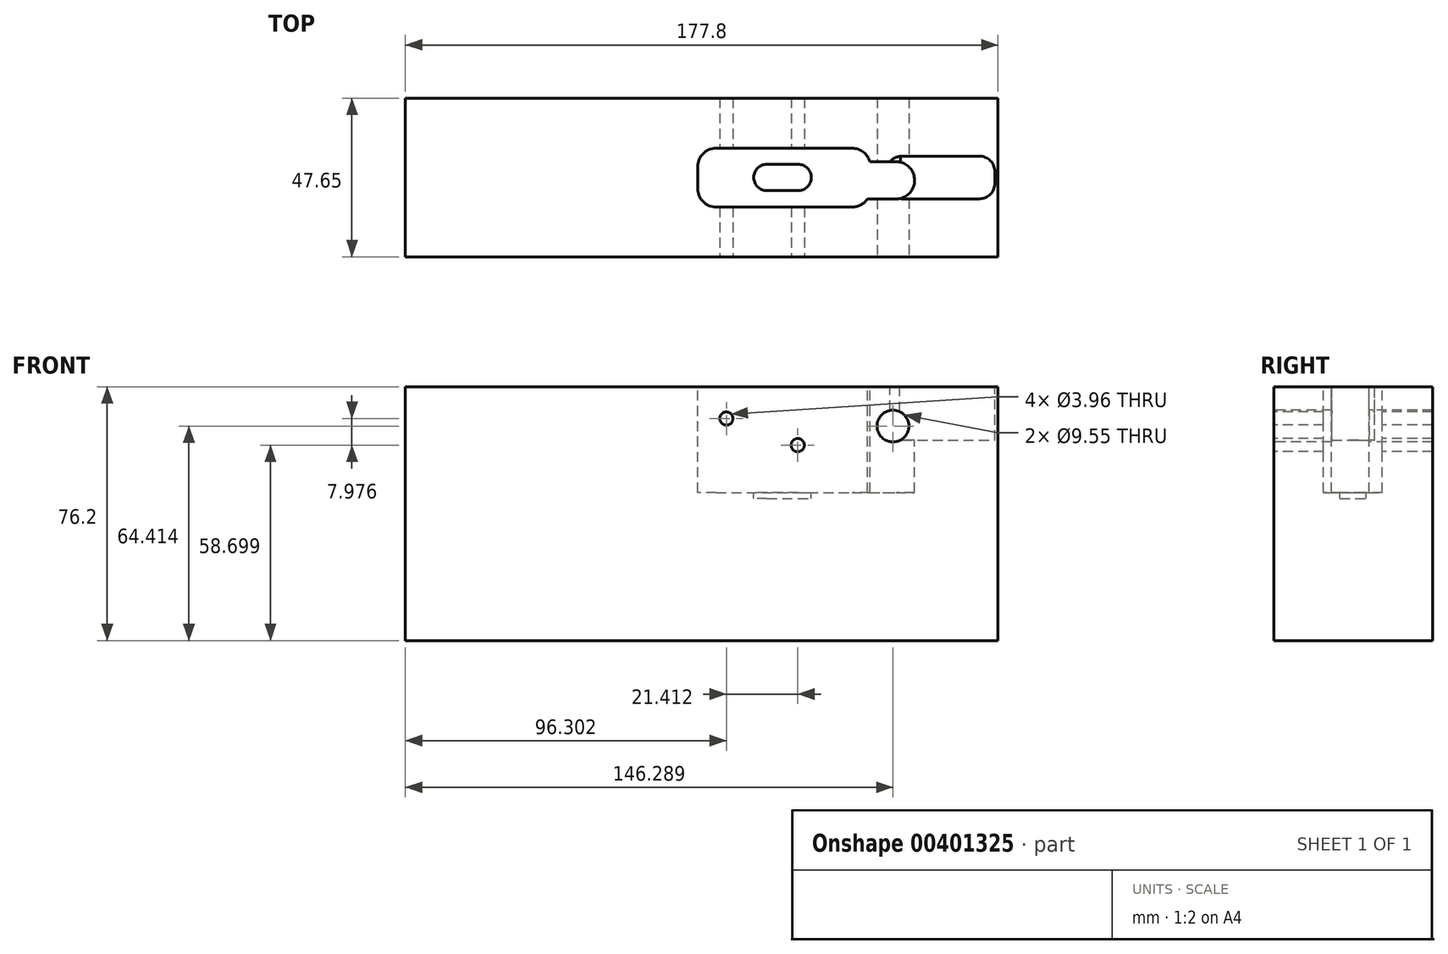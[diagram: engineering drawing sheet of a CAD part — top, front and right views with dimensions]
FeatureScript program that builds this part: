
annotation { "Feature Type Name" : "Feature", "Feature Type Description" : "" }
export const myFeature = defineFeature(function(context is Context, id is Id, definition is map)
    precondition{}
    {
        {
            var Q0;
            Q0=qCreatedBy(makeId("Top.planeOp"),FACE);
            var sketch = newSketch(context, id + "F0", { "sketchPlane" : qUnion([Q0])});
            skLineSegment(sketch, "E0.bottom", {"start": v(-4.76, 47.65) * mm, "end": v(173.04, 47.65) * mm});
            skLineSegment(sketch, "E0.top", {"start": v(-4.76, 0) * mm, "end": v(173.04, 0) * mm});
            skLineSegment(sketch, "E0.left", {"start": v(-4.76, 47.65) * mm, "end": v(-4.76, 0) * mm});
            skLineSegment(sketch, "E0.right", {"start": v(173.04, 47.65) * mm, "end": v(173.04, 0) * mm});
            skLineSegment(sketch, "E1", {"start": v(173, 23.83) * mm, "end": v(-20.73, 23.83) * mm, "construction": true});
            skPoint(sketch, "E1.startSnap0", {"position": v(173.04, 23.83) * mm});
            skPoint(sketch, "E1.endSnap0", {"position": v(-4.76, 23.83) * mm});
            skSolve(sketch);
        }
        {
            var Q0;
            Q0=makeQuery(id+"F0.imprint","IMPRINT",FACE,{"disambiguationData":[TD([[makeQuery(id+"F0.imprint","IMPRINT",EDGE,{"derivedFrom":sQuery(id+"F0.wireOp",EDGE,"E0.bottom")}),-1.0]])]});
            extrude(context, id + "F1", {"entities" : qUnion([Q0]), "oppositeDirection" : true, "depth" : 76.2 * mm});
        }
        {
            var Q0;
            Q0=qCreatedBy(makeId("Front.planeOp"),FACE);
            var sketch = newSketch(context, id + "F2", { "sketchPlane" : qUnion([Q0])});
            skCircle(sketch, "E2", {"center": v(0, 0) * mm, "radius": 3.18 * mm, "construction": true});
            skCircle(sketch, "E3", {"center": v(141.53, -11.79) * mm, "radius": 4.78 * mm});
            skCircle(sketch, "E4", {"center": v(112.95, -17.5) * mm, "radius": 1.98 * mm});
            skCircle(sketch, "E5", {"center": v(91.54, -9.52) * mm, "radius": 1.98 * mm});
            skSolve(sketch);
        }
        {
            var Q0;
            Q0=qSketchRegion(id+"F2",true);
            extrude(context, id + "F3", {"entities" : qUnion([Q0]), "operationType" : NewBodyOperationType.REMOVE, "endBound" : BoundingType.THROUGH_ALL, "oppositeDirection" : true, "depth" : 25.4 * mm});
        }
        {
            var Q0;
            Q0=makeQuery(id+"F0.imprint","IMPRINT",FACE,{"disambiguationData":[TD([[makeQuery(id+"F0.imprint","IMPRINT",EDGE,{"derivedFrom":sQuery(id+"F0.wireOp",EDGE,"E0.bottom")}),-1.0]])]});
            var sketch = newSketch(context, id + "F4", { "sketchPlane" : qUnion([Q0])});
            skLineSegment(sketch, "E6.right", {"start": v(172.14, 25.46) * mm, "end": v(172.14, 22.19) * mm});
            skPoint(sketch, "E7.visualSharp", {"position": v(172.14, 30.23) * mm});
            skPoint(sketch, "E8.visualSharp", {"position": v(172.14, 17.42) * mm});
            skPoint(sketch, "E9.visualSharp", {"position": v(142.53, 46.05) * mm});
            skLineSegment(sketch, "E10", {"start": v(144.26, 30.23) * mm, "end": v(167.37, 30.23) * mm});
            skLineSegment(sketch, "E11", {"start": v(0, 63.67) * mm, "end": v(0, 0) * mm, "construction": true});
            skLineSegment(sketch, "E12", {"start": v(139.5, 25.46) * mm, "end": v(139.5, 22.19) * mm});
            skLineSegment(sketch, "E13", {"start": v(144.26, 17.42) * mm, "end": v(167.37, 17.42) * mm});
            skPoint(sketch, "E14.visualSharp", {"position": v(139.5, 30.23) * mm});
            skPoint(sketch, "E15.visualSharp", {"position": v(139.5, 17.42) * mm});
            skArc(sketch, "E16.filletArc", {"start": v(144.26, 30.23) * mm, "mid": v(140.9, 28.83) * mm, "end": v(139.5, 25.46) * mm});
            skArc(sketch, "E17.filletArc", {"start": v(139.5, 22.19) * mm, "mid": v(140.9, 18.82) * mm, "end": v(144.26, 17.42) * mm});
            skArc(sketch, "E18.filletArc", {"start": v(167.37, 17.42) * mm, "mid": v(170.74, 18.82) * mm, "end": v(172.14, 22.19) * mm});
            skArc(sketch, "E19.filletArc", {"start": v(172.14, 25.46) * mm, "mid": v(170.74, 28.83) * mm, "end": v(167.37, 30.23) * mm});
            skSolve(sketch);
        }
        {
            var Q0;
            Q0=qSketchRegion(id+"F4",true);
            extrude(context, id + "F5", {"entities" : qUnion([Q0]), "operationType" : NewBodyOperationType.REMOVE, "oppositeDirection" : true, "depth" : 16 * mm});
        }
        {
            var Q0;
            Q0=makeQuery(id+"F0.imprint","IMPRINT",FACE,{"disambiguationData":[TD([[makeQuery(id+"F0.imprint","IMPRINT",EDGE,{"derivedFrom":sQuery(id+"F0.wireOp",EDGE,"E0.bottom")}),-1.0]])]});
            var sketch = newSketch(context, id + "F6", { "sketchPlane" : qUnion([Q0])});
            skLineSegment(sketch, "E20.bottom", {"start": v(103.7, 27.78) * mm, "end": v(113.06, 27.78) * mm});
            skLineSegment(sketch, "E20.top", {"start": v(103.7, 19.86) * mm, "end": v(113.06, 19.86) * mm});
            skLineSegment(sketch, "E20.left", {"start": v(99.75, 23.82) * mm, "end": v(99.75, 23.82) * mm});
            skLineSegment(sketch, "E20.right", {"start": v(117.02, 23.82) * mm, "end": v(117.02, 23.82) * mm});
            skPoint(sketch, "E21.visualSharp", {"position": v(99.75, 27.78) * mm});
            skArc(sketch, "E21.filletArc", {"start": v(103.7, 27.78) * mm, "mid": v(100.9, 26.62) * mm, "end": v(99.75, 23.82) * mm});
            skPoint(sketch, "E22.visualSharp", {"position": v(117.02, 27.78) * mm});
            skArc(sketch, "E22.filletArc", {"start": v(117.02, 23.82) * mm, "mid": v(115.86, 26.62) * mm, "end": v(113.06, 27.78) * mm});
            skPoint(sketch, "E23.visualSharp", {"position": v(117.02, 19.86) * mm});
            skArc(sketch, "E23.filletArc", {"start": v(113.06, 19.86) * mm, "mid": v(115.86, 21.02) * mm, "end": v(117.02, 23.82) * mm});
            skPoint(sketch, "E24.visualSharp", {"position": v(99.75, 19.86) * mm});
            skArc(sketch, "E24.filletArc", {"start": v(99.75, 23.82) * mm, "mid": v(100.9, 21.02) * mm, "end": v(103.7, 19.86) * mm});
            skSolve(sketch);
        }
        {
            var Q0;
            Q0=qSketchRegion(id+"F6",true);
            extrude(context, id + "F7", {"entities" : qUnion([Q0]), "operationType" : NewBodyOperationType.REMOVE, "oppositeDirection" : true, "depth" : 33.53 * mm});
        }
        {
            var Q0;
            Q0=qCreatedBy(makeId("Top.planeOp"),FACE);
            var sketch = newSketch(context, id + "F9", { "sketchPlane" : qUnion([Q0])});
            skLineSegment(sketch, "E25.bottom", {"start": v(134.6, 28.56) * mm, "end": v(142.47, 28.56) * mm});
            skLineSegment(sketch, "E25.top", {"start": v(133.84, 17.38) * mm, "end": v(142.47, 17.38) * mm});
            skLineSegment(sketch, "E25.right", {"start": v(148, 23.06) * mm, "end": v(148, 22.96) * mm});
            skPoint(sketch, "E26.visualSharp", {"position": v(147.96, 28.56) * mm});
            skArc(sketch, "E26.filletArc", {"start": v(148, 23.06) * mm, "mid": v(146.37, 26.95) * mm, "end": v(142.47, 28.56) * mm});
            skPoint(sketch, "E27.visualSharp", {"position": v(148.05, 17.38) * mm});
            skArc(sketch, "E27.filletArc", {"start": v(142.47, 17.38) * mm, "mid": v(146.4, 19.02) * mm, "end": v(148, 22.96) * mm});
            skPoint(sketch, "E28.visualSharp", {"position": v(131.4, 28.56) * mm});
            skPoint(sketch, "E29.visualSharp", {"position": v(131.4, 17.38) * mm});
            skLineSegment(sketch, "E30.bottom", {"start": v(88.47, 32.6) * mm, "end": v(129.26, 32.6) * mm});
            skLineSegment(sketch, "E30.top", {"start": v(88.47, 14.95) * mm, "end": v(129.26, 14.95) * mm});
            skLineSegment(sketch, "E30.left", {"start": v(82.93, 27.07) * mm, "end": v(82.93, 20.5) * mm});
            skArc(sketch, "E31.filletArc", {"start": v(134.6, 28.56) * mm, "mid": v(132.6, 31.48) * mm, "end": v(129.26, 32.6) * mm});
            skArc(sketch, "E32.filletArc", {"start": v(129.26, 14.95) * mm, "mid": v(131.85, 15.6) * mm, "end": v(133.84, 17.38) * mm});
            skArc(sketch, "E33.filletArc", {"start": v(88.47, 32.6) * mm, "mid": v(84.55, 30.99) * mm, "end": v(82.93, 27.07) * mm});
            skArc(sketch, "E34.filletArc", {"start": v(82.93, 20.5) * mm, "mid": v(84.55, 16.58) * mm, "end": v(88.47, 14.95) * mm});
            skLineSegment(sketch, "E35", {"start": v(53.04, 23.78) * mm, "end": v(165.2, 23.78) * mm, "construction": true});
            skLineSegment(sketch, "E36", {"start": v(129.26, 32.6) * mm, "end": v(129.26, 10.3) * mm, "construction": true});
            skSolve(sketch);
        }
        {
            var Q0;
            Q0=qSketchRegion(id+"F9",true);
            extrude(context, id + "F10", {"entities" : qUnion([Q0]), "operationType" : NewBodyOperationType.REMOVE, "oppositeDirection" : true, "depth" : 31.72 * mm});
        }
    });
